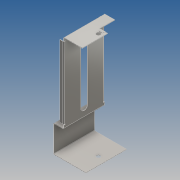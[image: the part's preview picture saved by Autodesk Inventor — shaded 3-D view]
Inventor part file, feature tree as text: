
AUTODESK INVENTOR PART (.ipt)
format: ipt  version: 2016 (Build 200138000, 138)  size: 209,408 bytes
history: native  units: mm
features: sheet_metal_op x10, sketch x8, other x7
ambient origin geometry x8: Origin, YZ Plane, XZ Plane, XY Plane, X Axis, Y Axis, Z Axis, Center Point
bodies: Solid1 (feature_tree)
feature tree (25):
  sheet_metal_op  "Contour Flange1"
  sheet_metal_op  "Flange1"
  sheet_metal_op  "Flange2"
  sheet_metal_op  "Hem1"
  sketch  "Sketch1"  dims[d0=105.0mm]
  other  "Plate1"
  sheet_metal_op  "Bend1"
  sheet_metal_op  "Corner1"
  sketch  "Sketch2"  dims[d1=27.0mm]
  sketch  "Sketch3"  dims[d2=78.0mm]
  other  "Plate2"
  sheet_metal_op  "Bend2"
  sheet_metal_op  "Corner2"
  sketch  "Sketch4"  dims[d3=18.5mm]
  other  "Plate3"
  sheet_metal_op  "Bend3"
  sheet_metal_op  "Corner3"
  sketch  "Sketch5"  dims[d4=9.8mm]
  sketch  "Sketch7"  dims[d6=0.25mm]
  sketch  "Sketch8"  dims[d7=1.0mm d8=0.5mm d9=40.0mm d10=0.5mm d11=0.5mm d12=2.0mm d13=0.5mm d14=0.5mm d15=7.0mm d16=60.0mm d17=0.5mm d18=0.0mm d19=0.5mm d20=0.25mm d21=1.0mm d22=0.5mm d23=4.0mm d24=90.0deg d25=0.5mm d26=3.0mm d27=3.0mm d28=2.0mm d29=0.5mm d30=0.5mm d31=0.5mm d32=0.25mm d33=1.0mm d34=0.5mm d35=3.0mm d36=3.0mm d37=4.0mm d38=90.0deg d39=0.5mm d40=2.0mm d41=0.5mm d42=0.5mm d43=8.0mm d44=15.0mm d45=0.5mm d46=0.0mm d47=0.5mm d48=0.25mm d49=1.0mm d50=0.5mm d51=2.0mm d52=2.0mm d53=3.0mm d54=0.25mm d55=0.125mm d56=4.0mm d57=0.5mm d58=0.0mm d59=0.5mm d60=0.0mm]
  other  "Cut1"
  other  "Cut2"
  other  "Cut3"
  other  "Cut4"
  sketch  "Sketch6"  dims[d5=0.5mm]
